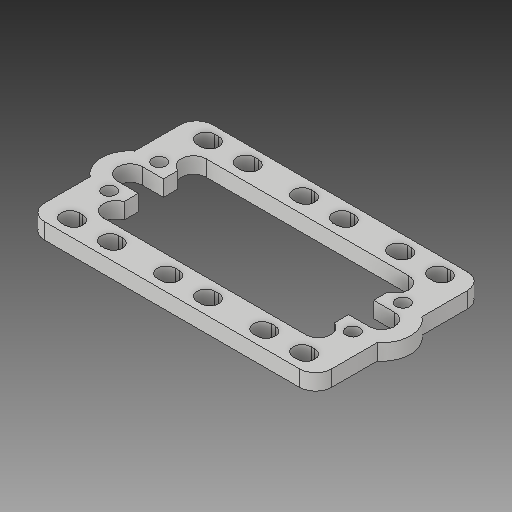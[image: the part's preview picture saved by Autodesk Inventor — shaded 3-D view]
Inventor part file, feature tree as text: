
AUTODESK INVENTOR PART (.ipt)
format: ipt  version: 2017 (Build 210142000, 142)  size: 181,760 bytes
history: native  units: in
note: dims shown in document units (in); Inventor stores cm internally (conversion verified against a paired STEP export)
features: mirror x1
ambient origin geometry x8: Origin, YZ Plane, XZ Plane, XY Plane, X Axis, Y Axis, Z Axis, Center Point
bodies: Solid1 (feature_tree)
feature tree (1):
  mirror  "Mirror2"
